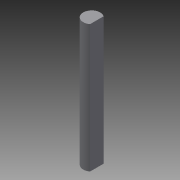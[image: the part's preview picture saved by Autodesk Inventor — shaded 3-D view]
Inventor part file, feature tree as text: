
AUTODESK INVENTOR PART (.ipt)
format: ipt  version: 2015 SP1 (Build 190203100, 203)  size: 69,632 bytes
history: native  units: in
note: dims shown in document units (in); Inventor stores cm internally (conversion verified against a paired STEP export)
features: extrude x1, sketch x1
ambient origin geometry x8: Origin, YZ Plane, XZ Plane, XY Plane, X Axis, Y Axis, Z Axis, Center Point
bodies: Solid1 (feature_tree)
feature tree (2):
  extrude  "Extrusion1"  Depth=30.0in TaperAngle=0.0deg
  sketch  "Sketch1"  dims[d0=2.0in d2=30.0in d3=0.0in d4=1.2in]
